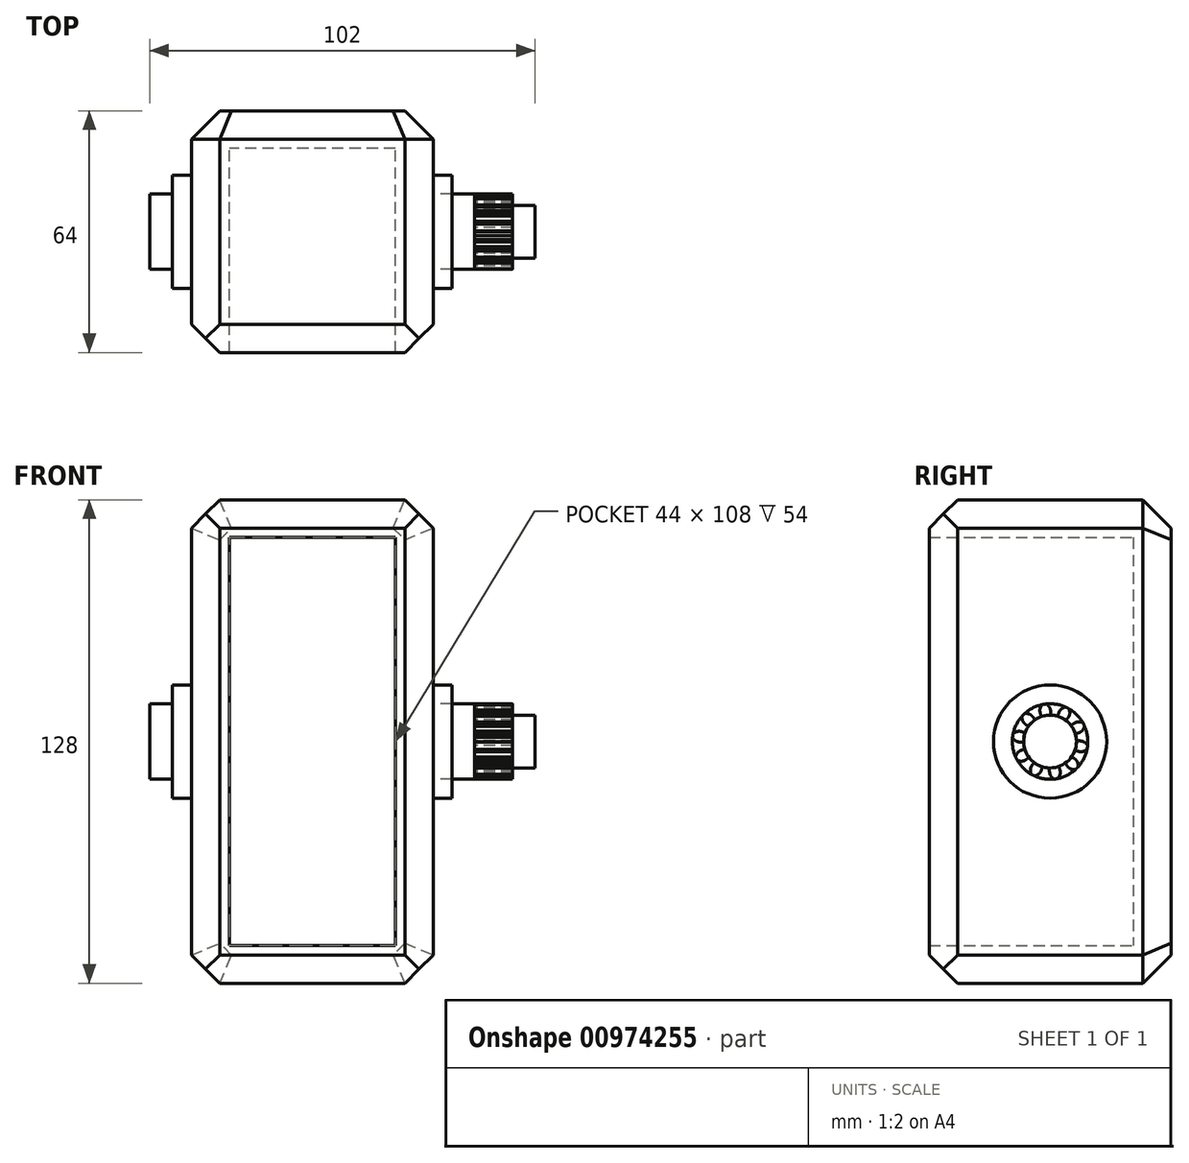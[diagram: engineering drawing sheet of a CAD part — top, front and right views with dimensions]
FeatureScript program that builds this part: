
annotation { "Feature Type Name" : "Feature", "Feature Type Description" : "" }
export const myFeature = defineFeature(function(context is Context, id is Id, definition is map)
    precondition{}
    {
        {
            var Q0;
            Q0=qCreatedBy(makeId("Front.planeOp"),FACE);
            var sketch = newSketch(context, id + "F0", { "sketchPlane" : qUnion([Q0])});
            skLineSegment(sketch, "E0.bottom", {"start": v(22, 54) * mm, "end": v(-22, 54) * mm});
            skLineSegment(sketch, "E0.top", {"start": v(22, -54) * mm, "end": v(-22, -54) * mm});
            skLineSegment(sketch, "E0.left", {"start": v(22, 54) * mm, "end": v(22, -54) * mm});
            skLineSegment(sketch, "E0.right", {"start": v(-22, 54) * mm, "end": v(-22, -54) * mm});
            skPoint(sketch, "E0.middle", {"position": v(0, 0) * mm});
            skLineSegment(sketch, "E1.bottom", {"start": v(32, 64) * mm, "end": v(-32, 64) * mm});
            skLineSegment(sketch, "E1.top", {"start": v(32, -64) * mm, "end": v(-32, -64) * mm});
            skLineSegment(sketch, "E1.left", {"start": v(32, 64) * mm, "end": v(32, -64) * mm});
            skLineSegment(sketch, "E1.right", {"start": v(-32, 64) * mm, "end": v(-32, -64) * mm});
            skSolve(sketch);
        }
        {
            var Q0;
            Q0=makeQuery(id+"F0.imprint","IMPRINT",FACE,{"disambiguationData":[TD([[makeQuery(id+"F0.imprint","IMPRINT",EDGE,{"derivedFrom":sQuery(id+"F0.wireOp",EDGE,"E0.bottom")}),1.0]])]});
            extrude(context, id + "F1", {"entities" : qUnion([Q0]), "depth" : 10 * mm, "offsetDistance" : 25 * mm});
        }
        {
            var Q0;
            Q0=makeQuery(id+"F0.imprint","IMPRINT",FACE,{"disambiguationData":[TD([[makeQuery(id+"F0.imprint","IMPRINT",EDGE,{"derivedFrom":sQuery(id+"F0.wireOp",EDGE,"E0.bottom")}),-1.0]])]});
            extrude(context, id + "F2", {"entities" : qUnion([Q0]), "operationType" : NewBodyOperationType.ADD, "depth" : 64 * mm, "offsetDistance" : 25 * mm});
        }
        {
            var Q0;
            Q0=makeQuery(id+"F2.opExtrude","SWEPT_EDGE",EDGE,{"disambiguationData":[OSD([sQuery(id+"F0.wireOp",EDGE,"E1.bottom"),sQuery(id+"F0.wireOp",EDGE,"E1.left")])]});
            var Q1;
            Q1=makeQuery(id+"F2.opExtrude","SWEPT_EDGE",EDGE,{"disambiguationData":[OSD([sQuery(id+"F0.wireOp",EDGE,"E1.bottom"),sQuery(id+"F0.wireOp",EDGE,"E1.right")])]});
            var Q2;
            Q2=makeQuery(id+"F2.opExtrude","SWEPT_EDGE",EDGE,{"disambiguationData":[OSD([sQuery(id+"F0.wireOp",EDGE,"E1.top"),sQuery(id+"F0.wireOp",EDGE,"E1.left")])]});
            var Q3;
            Q3=makeQuery(id+"F2.opExtrude","SWEPT_EDGE",EDGE,{"disambiguationData":[OSD([sQuery(id+"F0.wireOp",EDGE,"E1.top"),sQuery(id+"F0.wireOp",EDGE,"E1.right")])]});
            chamfer(context, id + "F3", {"entities" : qUnion([Q0, Q1, Q2, Q3]), "width" : 7.5 * mm, "tangentPropagation" : true});
        }
        {
            var Q0;
            Q0=makeQuery(id+"F2.opExtrude","CAP_EDGE",EDGE,{"disambiguationData":[OSD([sQuery(id+"F0.wireOp",EDGE,"E1.left")])],"isStart":true});
            var Q1;
            Q1=makeQuery(id+"F2.opExtrude","CAP_EDGE",EDGE,{"disambiguationData":[OSD([sQuery(id+"F0.wireOp",EDGE,"E1.right")])],"isStart":true});
            var Q2;
            Q2=makeQuery(id+"F2.opExtrude","CAP_EDGE",EDGE,{"disambiguationData":[OSD([sQuery(id+"F0.wireOp",EDGE,"E1.bottom")])],"isStart":true});
            var Q3;
            {var subQ0=sQuery(id+"F0.wireOp",EDGE,"E0.right");var subQ1=sQuery(id+"F0.wireOp",EDGE,"E0.left");var subQ2=sQuery(id+"F0.wireOp",EDGE,"E0.top");var subQ3=sQuery(id+"F0.wireOp",EDGE,"E0.bottom");Q3=makeQuery(id+"F2.boolean.opBoolean","MERGE",FACE,{"derivedFrom":[makeQuery(id+"F1.opExtrude","CAP_FACE",FACE,{"disambiguationData":[OSD([subQ3,subQ2,subQ1,subQ0])],"isStart":true}),makeQuery(id+"F2.opExtrude","CAP_FACE",FACE,{"disambiguationData":[OSD([subQ3,subQ2,subQ1,subQ0,sQuery(id+"F0.wireOp",EDGE,"E1.bottom"),sQuery(id+"F0.wireOp",EDGE,"E1.top"),sQuery(id+"F0.wireOp",EDGE,"E1.left"),sQuery(id+"F0.wireOp",EDGE,"E1.right")])],"isStart":true})]});}
            var Q4;
            Q4=makeQuery(id+"F2.opExtrude","CAP_EDGE",EDGE,{"disambiguationData":[OSD([sQuery(id+"F0.wireOp",EDGE,"E1.right")])],"isStart":false});
            var Q5;
            Q5=makeQuery(id+"F2.opExtrude","CAP_EDGE",EDGE,{"disambiguationData":[OSD([sQuery(id+"F0.wireOp",EDGE,"E1.top")])],"isStart":false});
            var Q6;
            Q6=makeQuery(id+"F2.opExtrude","CAP_EDGE",EDGE,{"disambiguationData":[OSD([sQuery(id+"F0.wireOp",EDGE,"E1.left")])],"isStart":false});
            var Q7;
            Q7=makeQuery(id+"F2.opExtrude","CAP_EDGE",EDGE,{"disambiguationData":[OSD([sQuery(id+"F0.wireOp",EDGE,"E1.bottom")])],"isStart":false});
            chamfer(context, id + "F4", {"entities" : qUnion([Q0, Q1, Q2, Q3, Q4, Q5, Q6, Q7]), "width" : 7.5 * mm, "tangentPropagation" : true});
        }
        {
            var Q0;
            Q0=makeQuery(id+"F1.opExtrude","SWEPT_BODY",BODY,{"disambiguationData":[OSD([sQuery(id+"F0.wireOp",EDGE,"E0.bottom"),sQuery(id+"F0.wireOp",EDGE,"E0.top"),sQuery(id+"F0.wireOp",EDGE,"E0.left"),sQuery(id+"F0.wireOp",EDGE,"E0.right")])]});
            transform(context, id + "F5", {"entities" : qUnion([Q0]), "transformType" : TransformType.TRANSLATION_3D, "dx" : 0 * mm, "dy" : 32 * mm, "dz" : 0 * mm, "makeCopy" : false});
        }
        {
            var Q0;
            Q0=makeQuery(id+"F2.opExtrude","SWEPT_FACE",FACE,{"disambiguationData":[OSD([sQuery(id+"F0.wireOp",EDGE,"E1.left")])]});
            var sketch = newSketch(context, id + "F6", { "sketchPlane" : qUnion([Q0])});
            skCircle(sketch, "E2", {"center": v(0, 0) * mm, "radius": 10 * mm});
            skCircle(sketch, "E3", {"center": v(0, 0) * mm, "radius": 15 * mm});
            skSolve(sketch);
        }
        {
            var Q0;
            Q0=makeQuery(id+"F6.imprint","IMPRINT",FACE,{"disambiguationData":[TD([[makeQuery(id+"F6.imprint","IMPRINT",EDGE,{"derivedFrom":sQuery(id+"F6.wireOp",EDGE,"E2")}),-1.0]])]});
            var Q1;
            Q1=makeQuery(id+"F6.imprint","IMPRINT",FACE,{"disambiguationData":[TD([[makeQuery(id+"F6.imprint","IMPRINT",EDGE,{"derivedFrom":sQuery(id+"F6.wireOp",EDGE,"E2")}),1.0]])]});
            extrude(context, id + "F7", {"entities" : qUnion([Q0, Q1]), "depth" : 5 * mm, "offsetDistance" : 25 * mm});
        }
        {
            var Q0;
            Q0=makeQuery(id+"F6.imprint","IMPRINT",FACE,{"disambiguationData":[TD([[makeQuery(id+"F6.imprint","IMPRINT",EDGE,{"derivedFrom":sQuery(id+"F6.wireOp",EDGE,"E2")}),1.0]])]});
            extrude(context, id + "F8", {"entities" : qUnion([Q0]), "depth" : 11 * mm, "offsetDistance" : 25 * mm});
        }
        {
            var Q0;
            Q0=makeQuery(id+"F2.opExtrude","SWEPT_FACE",FACE,{"disambiguationData":[OSD([sQuery(id+"F0.wireOp",EDGE,"E1.right")])]});
            var sketch = newSketch(context, id + "F9", { "sketchPlane" : qUnion([Q0])});
            skCircle(sketch, "E4", {"center": v(0, 0) * mm, "radius": 10 * mm});
            skCircle(sketch, "E5", {"center": v(0, 0) * mm, "radius": 15 * mm});
            skSolve(sketch);
        }
        {
            var Q0;
            Q0=makeQuery(id+"F9.imprint","IMPRINT",FACE,{"disambiguationData":[TD([[makeQuery(id+"F9.imprint","IMPRINT",EDGE,{"derivedFrom":sQuery(id+"F9.wireOp",EDGE,"E4")}),-1.0]])]});
            extrude(context, id + "F10", {"entities" : qUnion([Q0]), "operationType" : NewBodyOperationType.ADD, "depth" : 5 * mm, "offsetDistance" : 25 * mm});
        }
        {
            var Q0;
            Q0=makeQuery(id+"F10.boolean.opBoolean","SPLIT",FACE,{"disambiguationData":[TD([makeQuery(id+"F10.opExtrude","SWEPT_FACE",FACE,{"disambiguationData":[OSD([sQuery(id+"F9.wireOp",EDGE,"E4")])]})])],"derivedFrom":makeQuery(id+"F2.opExtrude","SWEPT_FACE",FACE,{"disambiguationData":[OSD([sQuery(id+"F0.wireOp",EDGE,"E1.right")])]})});
            extrude(context, id + "F11", {"entities" : qUnion([Q0]), "operationType" : NewBodyOperationType.ADD, "depth" : 11 * mm, "offsetDistance" : 25 * mm});
        }
        {
            var Q0;
            Q0=makeQuery(id+"F8.opExtrude","CAP_FACE",FACE,{"disambiguationData":[OSD([sQuery(id+"F6.wireOp",EDGE,"E2")])],"isStart":false});
            var sketch = newSketch(context, id + "F12", { "sketchPlane" : qUnion([Q0])});
            skCircle(sketch, "E6", {"center": v(0, 0) * mm, "radius": 10 * mm, "construction": true});
            skCircle(sketch, "E7", {"center": v(0, 0) * mm, "radius": 7 * mm});
            skCircle(sketch, "E8", {"center": v(0, 0) * mm, "radius": 8.75 * mm, "construction": true});
            skLineSegment(sketch, "E9", {"start": v(0, 0) * mm, "end": v(0, 12.26) * mm, "construction": true});
            skLineSegment(sketch, "E10", {"start": v(0, 0) * mm, "end": v(-1.82, 11.47) * mm, "construction": true});
            skLineSegment(sketch, "E11", {"start": v(0, 8.75) * mm, "end": v(-6.97, 8.75) * mm, "construction": true});
            skLineSegment(sketch, "E12", {"start": v(0, 8.75) * mm, "end": v(-6.6, 6.35) * mm, "construction": true});
            skCircle(sketch, "E13", {"center": v(0, 0) * mm, "radius": 8.22 * mm, "construction": true});
            skCircle(sketch, "E14", {"center": v(0, 8.75) * mm, "radius": 2.2 * mm, "construction": true});
            skCircle(sketch, "E15", {"center": v(-2.05, 7.96) * mm, "radius": 2.2 * mm, "construction": true});
            skArc(sketch, "E16", {"start": v(0, 8.75) * mm, "mid": v(-0.44, 9.45) * mm, "end": v(-1.1, 9.94) * mm});
            skArc(sketch, "E17", {"start": v(0.13, 8.22) * mm, "mid": v(0.08, 8.49) * mm, "end": v(0, 8.75) * mm});
            skArc(sketch, "E18", {"start": v(0.13, 7) * mm, "mid": v(0.16, 7.61) * mm, "end": v(0.13, 8.22) * mm});
            skArc(sketch, "E19.MirrorCS", {"start": v(-2.67, 7.78) * mm, "mid": v(-2.7, 8.05) * mm, "end": v(-2.7, 8.32) * mm});
            skArc(sketch, "E20.MirrorCS", {"start": v(-2.7, 8.32) * mm, "mid": v(-2.5, 9.12) * mm, "end": v(-2.02, 9.8) * mm});
            skArc(sketch, "E21.MirrorCS", {"start": v(-2.29, 6.62) * mm, "mid": v(-2.5, 7.19) * mm, "end": v(-2.67, 7.78) * mm});
            skArc(sketch, "E22", {"start": v(-1.1, 9.94) * mm, "mid": v(-1.56, 9.88) * mm, "end": v(-2.02, 9.8) * mm});
            skSolve(sketch);
        }
        {
            var Q0;
            {var subQ0=sQuery(id+"F12.wireOp",EDGE,"E7");var subQ1=makeQuery(id+"F12.imprint","INTERSECT",VERTEX,{"derivedFrom":[subQ0,sQuery(id+"F12.wireOp",EDGE,"E18")]});Q0=makeQuery(id+"F12.imprint","IMPRINT",FACE,{"disambiguationData":[TD([[makeQuery(id+"F12.imprint","IMPRINT",EDGE,{"disambiguationData":[TD([[subQ1,-1.0]])],"derivedFrom":subQ0}),1.0]])]});}
            var Q1;
            {var subQ1=sQuery(id+"F12.wireOp",EDGE,"E16");Q1=makeQuery(id+"F12.imprint","IMPRINT",FACE,{"disambiguationData":[TD([[makeQuery(id+"F12.imprint","IMPRINT",EDGE,{"derivedFrom":subQ1}),1.0]])]});}
            extrude(context, id + "F13", {"entities" : qUnion([Q0, Q1]), "depth" : 10 * mm, "offsetDistance" : 25 * mm});
        }
        {
            var Q0;
            Q0=makeQuery(id+"F13.opExtrude","SWEPT_BODY",BODY,{"disambiguationData":[OSD([sQuery(id+"F6.wireOp",EDGE,"E2"),sQuery(id+"F12.wireOp",EDGE,"E7"),sQuery(id+"F12.wireOp",EDGE,"E16"),sQuery(id+"F12.wireOp",EDGE,"E17"),sQuery(id+"F12.wireOp",EDGE,"E18"),sQuery(id+"F12.wireOp",EDGE,"E19.MirrorCS"),sQuery(id+"F12.wireOp",EDGE,"E20.MirrorCS"),sQuery(id+"F12.wireOp",EDGE,"E21.MirrorCS")])]});
            var Q1;
            Q1=makeQuery(id+"F13.opExtrude","SWEPT_FACE",FACE,{"disambiguationData":[OSD([sQuery(id+"F12.wireOp",EDGE,"E7")])]});
            circularPattern(context, id + "F14", {"entities" : qUnion([Q0]), "axis" : qUnion([Q1]), "angle" : 360 * degree, "instanceCount" : 10, "equalSpace" : true});
        }
        {
            var Q0;
            Q0=makeQuery(id+"F13.opExtrude","CAP_FACE",FACE,{"disambiguationData":[OSD([sQuery(id+"F6.wireOp",EDGE,"E2"),sQuery(id+"F12.wireOp",EDGE,"E7"),sQuery(id+"F12.wireOp",EDGE,"E16"),sQuery(id+"F12.wireOp",EDGE,"E17"),sQuery(id+"F12.wireOp",EDGE,"E18"),sQuery(id+"F12.wireOp",EDGE,"E19.MirrorCS"),sQuery(id+"F12.wireOp",EDGE,"E20.MirrorCS"),sQuery(id+"F12.wireOp",EDGE,"E21.MirrorCS")])],"isStart":false});
            var sketch = newSketch(context, id + "F15", { "sketchPlane" : qUnion([Q0])});
            skCircle(sketch, "E23", {"center": v(0, 0) * mm, "radius": 7 * mm});
            skSolve(sketch);
        }
        {
            var Q0;
            {var subQ0=sQuery(id+"F15.wireOp",EDGE,"E23");var subQ1=makeQuery(id+"F15.imprint","INTERSECT",VERTEX,{"derivedFrom":[makeQuery(id+"F13.opExtrude","CAP_EDGE",EDGE,{"disambiguationData":[OSD([sQuery(id+"F12.wireOp",EDGE,"E18")])],"isStart":false}),subQ0]});Q0=makeQuery(id+"F15.imprint","IMPRINT",FACE,{"disambiguationData":[TD([[makeQuery(id+"F15.imprint","IMPRINT",EDGE,{"disambiguationData":[TD([[subQ1,-1.0]])],"derivedFrom":subQ0}),1.0]])]});}
            extrude(context, id + "F16", {"entities" : qUnion([Q0]), "depth" : 6 * mm, "offsetDistance" : 25 * mm});
        }
    });
